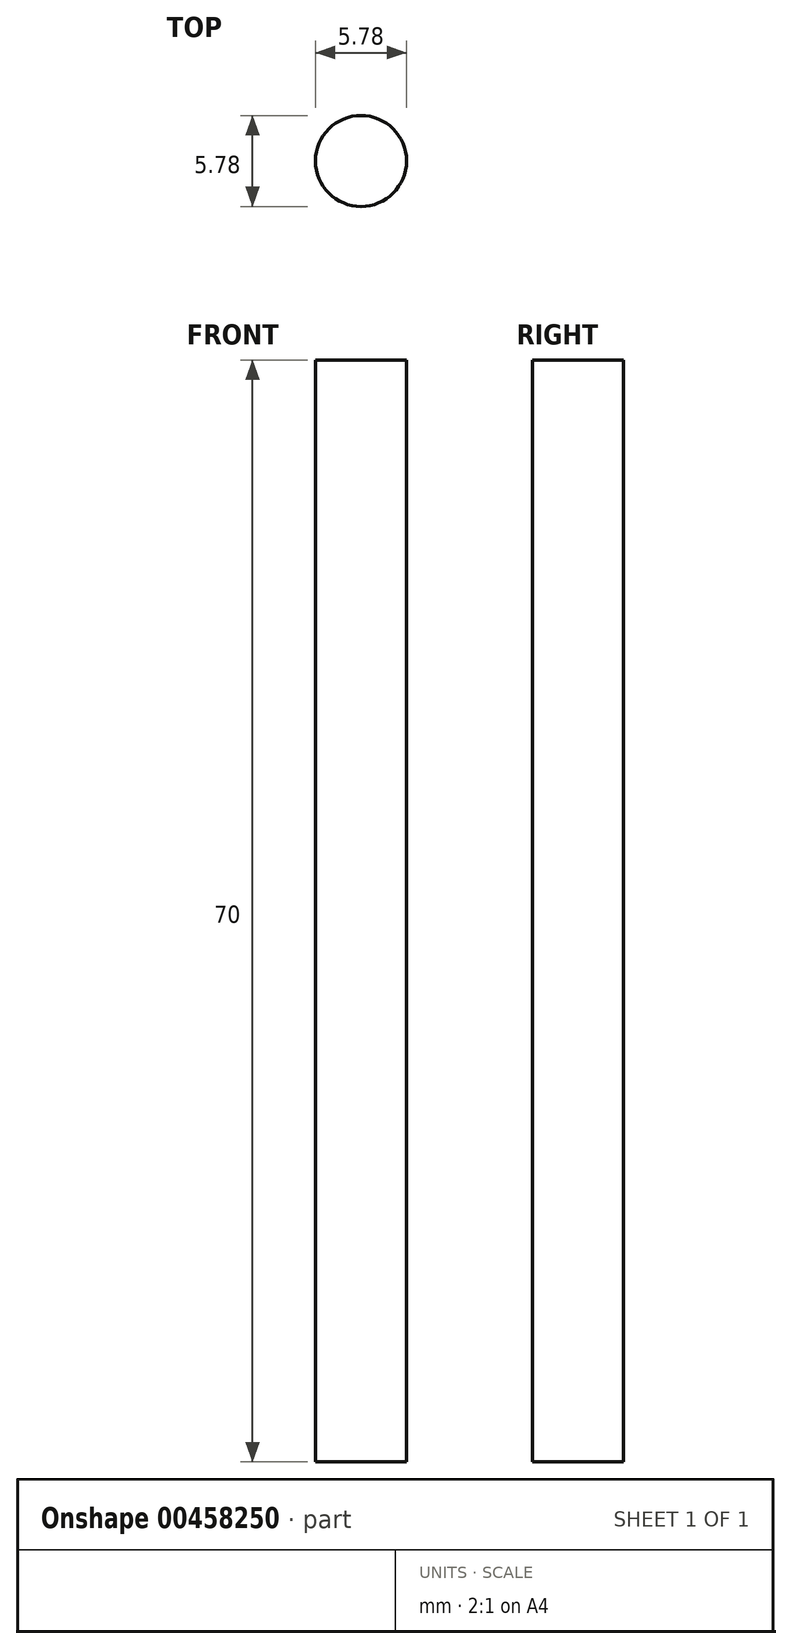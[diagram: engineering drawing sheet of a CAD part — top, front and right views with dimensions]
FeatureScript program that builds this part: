
annotation { "Feature Type Name" : "Feature", "Feature Type Description" : "" }
export const myFeature = defineFeature(function(context is Context, id is Id, definition is map)
    precondition{}
    {
        {
            var Q0;
            Q0=qCreatedBy(makeId("Top.planeOp"),FACE);
            var sketch = newSketch(context, id + "F0", { "sketchPlane" : qUnion([Q0])});
            skCircle(sketch, "E0", {"center": v(0, 0) * mm, "radius": 2.9 * mm});
            skSolve(sketch);
        }
        {
            var Q0;
            Q0=makeQuery(id+"F0.imprint","IMPRINT",FACE,{"disambiguationData":[TD([[makeQuery(id+"F0.imprint","IMPRINT",EDGE,{"derivedFrom":sQuery(id+"F0.wireOp",EDGE,"E0")}),1.0]])]});
            extrude(context, id + "F1", {"entities" : qUnion([Q0]), "depth" : 70 * mm});
        }
    });
